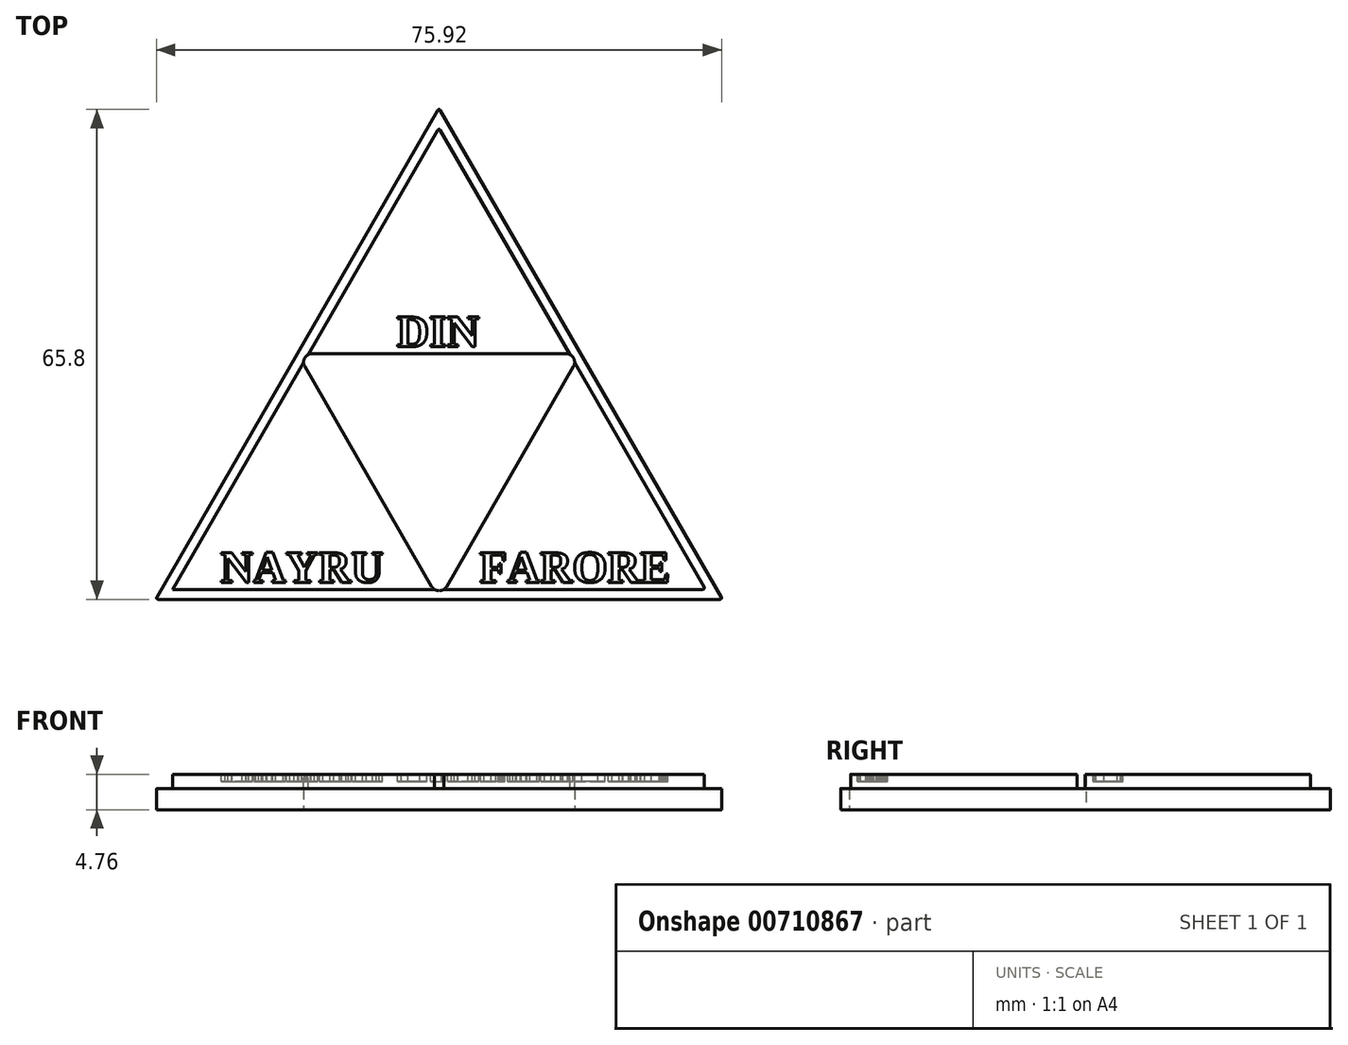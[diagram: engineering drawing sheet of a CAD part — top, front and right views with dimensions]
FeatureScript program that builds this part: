
annotation { "Feature Type Name" : "Feature", "Feature Type Description" : "" }
export const myFeature = defineFeature(function(context is Context, id is Id, definition is map)
    precondition{}
    {
        {
            var Q0;
            Q0=qCreatedBy(makeId("Top.planeOp"),FACE);
            var sketch = newSketch(context, id + "F0", { "sketchPlane" : qUnion([Q0])});
            skLineSegment(sketch, "E0", {"start": v(-0.1, -0.2) * mm, "end": v(-12.7, -22) * mm});
            skLineSegment(sketch, "E1", {"start": v(-11.38, -22) * mm, "end": v(11.38, -22) * mm});
            skLineSegment(sketch, "E2", {"start": v(12.7, -22) * mm, "end": v(0.1, -0.2) * mm});
            skLineSegment(sketch, "E3", {"start": v(-12.7, -22) * mm, "end": v(-25.3, -43.8) * mm});
            skLineSegment(sketch, "E4", {"start": v(-25.18, -44) * mm, "end": v(0, -44) * mm});
            skLineSegment(sketch, "E5", {"start": v(-0.66, -42.85) * mm, "end": v(-12.04, -23.14) * mm});
            skLineSegment(sketch, "E6", {"start": v(0.66, -42.85) * mm, "end": v(12.04, -23.14) * mm});
            skLineSegment(sketch, "E7", {"start": v(25.3, -43.8) * mm, "end": v(12.7, -22) * mm});
            skLineSegment(sketch, "E8", {"start": v(0, -44) * mm, "end": v(25.18, -44) * mm});
            skPoint(sketch, "E9.visualSharp", {"position": v(-12.7, -22) * mm});
            skArc(sketch, "E9.filletArc", {"start": v(-11.38, -22) * mm, "mid": v(-12.04, -22.38) * mm, "end": v(-12.04, -23.14) * mm});
            skPoint(sketch, "E10.visualSharp", {"position": v(12.7, -22) * mm});
            skArc(sketch, "E10.filletArc", {"start": v(12.04, -23.14) * mm, "mid": v(12.04, -22.38) * mm, "end": v(11.38, -22) * mm});
            skPoint(sketch, "E11.visualSharp", {"position": v(0, -44) * mm});
            skArc(sketch, "E11.filletArc", {"start": v(-0.66, -42.85) * mm, "mid": v(0, -43.23) * mm, "end": v(0.66, -42.85) * mm});
            skPoint(sketch, "E12.visualSharp", {"position": v(0, 0) * mm});
            skArc(sketch, "E12.filletArc", {"start": v(0.01, -0.02) * mm, "mid": v(0, -0.01) * mm, "end": v(-0.01, -0.02) * mm});
            skPoint(sketch, "E13.visualSharp", {"position": v(25.4, -44) * mm});
            skArc(sketch, "E13.filletArc", {"start": v(25.18, -44) * mm, "mid": v(25.3, -43.93) * mm, "end": v(25.3, -43.8) * mm});
            skPoint(sketch, "E14.visualSharp", {"position": v(-25.4, -44) * mm});
            skArc(sketch, "E14.filletArc", {"start": v(-25.3, -43.8) * mm, "mid": v(-25.3, -43.93) * mm, "end": v(-25.18, -44) * mm});
            skArc(sketch, "E15.filletArc", {"start": v(0.1, -0.2) * mm, "mid": v(0, -0.13) * mm, "end": v(-0.1, -0.2) * mm});
            skSolve(sketch);
        }
        {
            var Q0;
            Q0=makeQuery(id+"F0.imprint","IMPRINT",FACE,{"disambiguationData":[TD([[makeQuery(id+"F0.imprint","IMPRINT",EDGE,{"derivedFrom":sQuery(id+"F0.wireOp",EDGE,"E0")}),1.0]])]});
            var Q1;
            Q1=makeQuery(id+"F0.imprint","IMPRINT",FACE,{"disambiguationData":[TD([[makeQuery(id+"F0.imprint","IMPRINT",EDGE,{"derivedFrom":sQuery(id+"F0.wireOp",EDGE,"E6")}),-1.0]])]});
            var Q2;
            Q2=makeQuery(id+"F0.imprint","IMPRINT",FACE,{"disambiguationData":[TD([[makeQuery(id+"F0.imprint","IMPRINT",EDGE,{"derivedFrom":sQuery(id+"F0.wireOp",EDGE,"E3")}),1.0]])]});
            extrude(context, id + "F1", {"entities" : qUnion([Q0, Q1, Q2]), "depth" : 3.17 * mm, "offsetDistance" : 25.4 * mm});
        }
        {
            var Q0;
            Q0=makeQuery(id+"F1.opExtrude","CAP_FACE",FACE,{"disambiguationData":[OSD([sQuery(id+"F0.wireOp",EDGE,"E0"),sQuery(id+"F0.wireOp",EDGE,"E1"),sQuery(id+"F0.wireOp",EDGE,"E2"),sQuery(id+"F0.wireOp",EDGE,"E3"),sQuery(id+"F0.wireOp",EDGE,"E4"),sQuery(id+"F0.wireOp",EDGE,"E5"),sQuery(id+"F0.wireOp",EDGE,"E6"),sQuery(id+"F0.wireOp",EDGE,"E7"),sQuery(id+"F0.wireOp",EDGE,"E8"),sQuery(id+"F0.wireOp",EDGE,"E9.filletArc"),sQuery(id+"F0.wireOp",EDGE,"E10.filletArc"),sQuery(id+"F0.wireOp",EDGE,"E11.filletArc"),sQuery(id+"F0.wireOp",EDGE,"E13.filletArc"),sQuery(id+"F0.wireOp",EDGE,"E14.filletArc"),sQuery(id+"F0.wireOp",EDGE,"E15.filletArc")])],"isStart":false});
            var sketch = newSketch(context, id + "F2", { "sketchPlane" : qUnion([Q0])});
            skLineSegment(sketch, "E16", {"start": v(0, 0) * mm, "end": v(-25.4, -44) * mm});
            skLineSegment(sketch, "E17", {"start": v(0, 0) * mm, "end": v(25.4, -44) * mm});
            skLineSegment(sketch, "E18", {"start": v(25.18, -44) * mm, "end": v(25.4, -44) * mm});
            skLineSegment(sketch, "E19.trimOffspring", {"start": v(25.4, -44) * mm, "end": v(-25.4, -44) * mm});
            skLineSegment(sketch, "E20.0", {"start": v(-23.64, -43.1) * mm, "end": v(23.64, -43.1) * mm});
            skLineSegment(sketch, "E20.1", {"start": v(-0.1, -1.97) * mm, "end": v(-23.75, -42.91) * mm});
            skLineSegment(sketch, "E20.2", {"start": v(23.75, -42.91) * mm, "end": v(0.1, -1.97) * mm});
            skLineSegment(sketch, "E21.trimOffspring", {"start": v(23.86, -43.1) * mm, "end": v(-23.86, -43.1) * mm});
            skLineSegment(sketch, "E22.trimOffspring", {"start": v(0, -1.78) * mm, "end": v(-23.86, -43.1) * mm});
            skPoint(sketch, "E23.visualSharp", {"position": v(0, -1.78) * mm});
            skArc(sketch, "E23.filletArc", {"start": v(0.1, -1.97) * mm, "mid": v(0, -1.9) * mm, "end": v(-0.1, -1.97) * mm});
            skPoint(sketch, "E24.visualSharp", {"position": v(23.86, -43.1) * mm});
            skArc(sketch, "E24.filletArc", {"start": v(23.64, -43.1) * mm, "mid": v(23.75, -43.04) * mm, "end": v(23.75, -42.91) * mm});
            skPoint(sketch, "E25.visualSharp", {"position": v(-23.86, -43.1) * mm});
            skArc(sketch, "E25.filletArc", {"start": v(-23.75, -42.91) * mm, "mid": v(-23.75, -43.04) * mm, "end": v(-23.64, -43.1) * mm});
            skSolve(sketch);
        }
        {
            var Q0;
            {var subQ8=sQuery(id+"F2.wireOp",EDGE,"E23.filletArc");Q0=makeQuery(id+"F2.imprint","IMPRINT",FACE,{"disambiguationData":[TD([[makeQuery(id+"F2.imprint","IMPRINT",EDGE,{"derivedFrom":subQ8}),-1.0]])]});}
            extrude(context, id + "F3", {"entities" : qUnion([Q0]), "operationType" : NewBodyOperationType.REMOVE, "oppositeDirection" : true, "depth" : 1.27 * mm, "offsetDistance" : 25.4 * mm});
        }
        {
            var Q0;
            {var subQ0=sQuery(id+"F0.wireOp",EDGE,"E1");Q0=makeQuery(id+"F3.boolean.opBoolean","SPLIT",FACE,{"disambiguationData":[TD([makeQuery(id+"F1.opExtrude","SWEPT_FACE",FACE,{"disambiguationData":[OSD([subQ0])]})])],"derivedFrom":makeQuery(id+"F1.opExtrude","CAP_FACE",FACE,{"disambiguationData":[OSD([sQuery(id+"F0.wireOp",EDGE,"E0"),subQ0,sQuery(id+"F0.wireOp",EDGE,"E2"),sQuery(id+"F0.wireOp",EDGE,"E3"),sQuery(id+"F0.wireOp",EDGE,"E4"),sQuery(id+"F0.wireOp",EDGE,"E5"),sQuery(id+"F0.wireOp",EDGE,"E6"),sQuery(id+"F0.wireOp",EDGE,"E7"),sQuery(id+"F0.wireOp",EDGE,"E8"),sQuery(id+"F0.wireOp",EDGE,"E9.filletArc"),sQuery(id+"F0.wireOp",EDGE,"E10.filletArc"),sQuery(id+"F0.wireOp",EDGE,"E11.filletArc"),sQuery(id+"F0.wireOp",EDGE,"E13.filletArc"),sQuery(id+"F0.wireOp",EDGE,"E14.filletArc"),sQuery(id+"F0.wireOp",EDGE,"E15.filletArc")])],"isStart":false})});}
            var sketch = newSketch(context, id + "F4", { "sketchPlane" : qUnion([Q0])});
            skText(sketch, "E26", { "text": "DIN", "fontName": "Tinos-Bold.ttf"});
            skText(sketch, "E27", { "text": "NAYRU", "fontName": "Tinos-Bold.ttf"});
            skPoint(sketch, "E28", {"position": v(-12.2, -19.41) * mm});
            skText(sketch, "E29", { "text": "FARORE", "fontName": "Tinos-Bold.ttf"});
            const initialGuessF4  = {"E26": [-0.00381, -0.02136, 1, 0, 0.00291], "E27": [-0.01957, -0.04247, 1, 0, 0.00291], "E29": [0.00363, -0.04247, 1, 0, 0.00291]};
            skSetInitialGuess(sketch, initialGuessF4);
            skSolve(sketch);
        }
        {
            var Q0;
            Q0=qSketchRegion(id+"F4",true);
            extrude(context, id + "F5", {"entities" : qUnion([Q0]), "operationType" : NewBodyOperationType.REMOVE, "oppositeDirection" : true, "depth" : 0.64 * mm, "offsetDistance" : 25.4 * mm});
        }
        {
            var Q0;
            Q0=makeQuery(id+"F1.opExtrude","SWEPT_BODY",BODY,{"disambiguationData":[OSD([sQuery(id+"F0.wireOp",EDGE,"E0"),sQuery(id+"F0.wireOp",EDGE,"E1"),sQuery(id+"F0.wireOp",EDGE,"E2"),sQuery(id+"F0.wireOp",EDGE,"E3"),sQuery(id+"F0.wireOp",EDGE,"E4"),sQuery(id+"F0.wireOp",EDGE,"E5"),sQuery(id+"F0.wireOp",EDGE,"E6"),sQuery(id+"F0.wireOp",EDGE,"E7"),sQuery(id+"F0.wireOp",EDGE,"E8"),sQuery(id+"F0.wireOp",EDGE,"E9.filletArc"),sQuery(id+"F0.wireOp",EDGE,"E10.filletArc"),sQuery(id+"F0.wireOp",EDGE,"E11.filletArc"),sQuery(id+"F0.wireOp",EDGE,"E13.filletArc"),sQuery(id+"F0.wireOp",EDGE,"E14.filletArc"),sQuery(id+"F0.wireOp",EDGE,"E15.filletArc")])]});
            var Q1;
            Q1=qCreatedBy(makeId("Origin.pointOp"),VERTEX);
            transform(context, id + "F6", {"entities" : qUnion([Q0]), "transformType" : TransformType.SCALE_UNIFORMLY, "scale" : 1.5, "scalePoint" : qUnion([Q1]), "makeCopy" : false});
        }
    });
